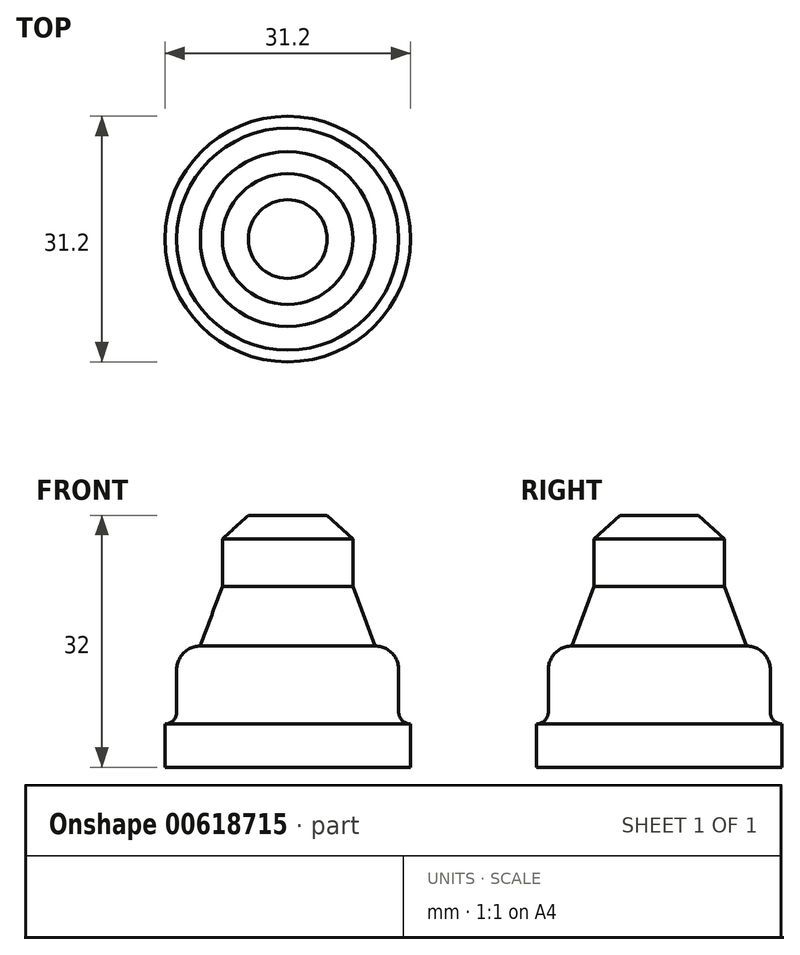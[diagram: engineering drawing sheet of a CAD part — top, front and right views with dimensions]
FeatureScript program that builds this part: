
annotation { "Feature Type Name" : "Feature", "Feature Type Description" : "" }
export const myFeature = defineFeature(function(context is Context, id is Id, definition is map)
    precondition{}
    {
        {
            var Q0;
            Q0=qCreatedBy(makeId("Front.planeOp"),FACE);
            var sketch = newSketch(context, id + "F0", { "sketchPlane" : qUnion([Q0])});
            skLineSegment(sketch, "E0", {"start": v(0, -16) * mm, "end": v(0, 16) * mm});
            skLineSegment(sketch, "E1", {"start": v(0, -16) * mm, "end": v(15.6, -16) * mm});
            skLineSegment(sketch, "E2", {"start": v(15.6, -16) * mm, "end": v(15.6, -10.5) * mm});
            skLineSegment(sketch, "E3", {"start": v(14.1, -9) * mm, "end": v(14.1, -3.6) * mm});
            skLineSegment(sketch, "E4", {"start": v(0, 16) * mm, "end": v(5, 16) * mm});
            skLineSegment(sketch, "E5", {"start": v(5, 16) * mm, "end": v(8.3, 13) * mm});
            skLineSegment(sketch, "E6", {"start": v(8.3, 13) * mm, "end": v(8.3, 7) * mm});
            skLineSegment(sketch, "E7", {"start": v(8.3, 7) * mm, "end": v(11.1, -0.6) * mm});
            skArc(sketch, "E8", {"start": v(14.1, -3.6) * mm, "mid": v(13.22, -1.48) * mm, "end": v(11.1, -0.6) * mm});
            skArc(sketch, "E9", {"start": v(14.1, -9) * mm, "mid": v(14.54, -10.06) * mm, "end": v(15.6, -10.5) * mm});
            skLineSegment(sketch, "E10", {"start": v(10.88, 0) * mm, "end": v(0, 0) * mm, "construction": true});
            skPoint(sketch, "E10.endSnap0", {"position": v(0, 0) * mm});
            skSolve(sketch);
        }
        {
            var Q0;
            Q0=makeQuery(id+"F0.imprint","IMPRINT",FACE,{"disambiguationData":[TD([[makeQuery(id+"F0.imprint","IMPRINT",EDGE,{"derivedFrom":sQuery(id+"F0.wireOp",EDGE,"E0")}),-1.0]])]});
            var Q1;
            Q1=sQuery(id+"F0.wireOp",EDGE,"E0");
            revolve(context, id + "F1", {"entities" : qUnion([Q0]), "axis" : qUnion([Q1]), "revolveType" : RevolveType.FULL});
        }
    });
